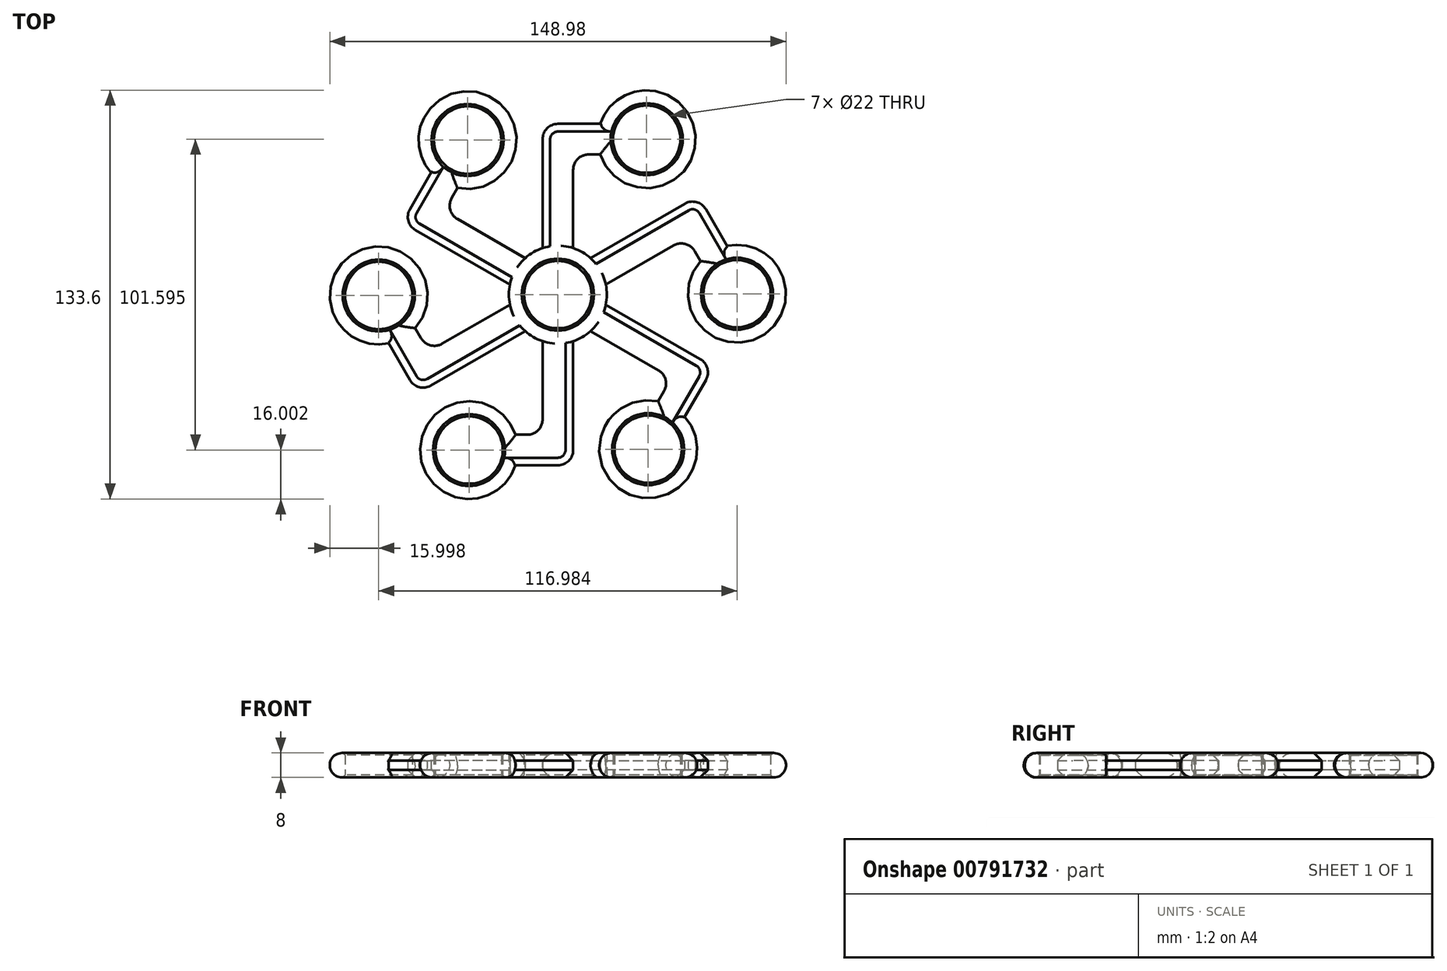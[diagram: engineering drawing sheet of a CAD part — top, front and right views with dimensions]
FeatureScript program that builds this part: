
annotation { "Feature Type Name" : "Feature", "Feature Type Description" : "" }
export const myFeature = defineFeature(function(context is Context, id is Id, definition is map)
    precondition{}
    {
        {
            var Q0;
            Q0=qCreatedBy(makeId("Top.planeOp"),FACE);
            var sketch = newSketch(context, id + "F0", { "sketchPlane" : qUnion([Q0])});
            skCircle(sketch, "E0", {"center": v(0, 0) * mm, "radius": 11 * mm});
            skCircle(sketch, "E1", {"center": v(0, 0) * mm, "radius": 16 * mm});
            skLineSegment(sketch, "E2", {"start": v(0, 0) * mm, "end": v(0, 50.8) * mm});
            skLineSegment(sketch, "E3", {"start": v(0, 50.8) * mm, "end": v(13, 50.8) * mm});
            skCircle(sketch, "E4", {"center": v(29, 50.8) * mm, "radius": 11 * mm});
            skCircle(sketch, "E5", {"center": v(29, 50.8) * mm, "radius": 16 * mm});
            skLineSegment(sketch, "E6.0", {"start": v(5, 15.2) * mm, "end": v(5, 40.8) * mm});
            skLineSegment(sketch, "E7.0", {"start": v(-5, 15.2) * mm, "end": v(-5, 50.8) * mm});
            skLineSegment(sketch, "E8.0", {"start": v(10, 45.8) * mm, "end": v(13.8, 45.8) * mm});
            skLineSegment(sketch, "E9.0", {"start": v(0, 55.8) * mm, "end": v(13.8, 55.8) * mm});
            skArc(sketch, "E10.filletArc", {"start": v(0, 55.8) * mm, "mid": v(-3.54, 54.33) * mm, "end": v(-5, 50.8) * mm});
            skArc(sketch, "E11.filletArc", {"start": v(10, 45.8) * mm, "mid": v(6.46, 44.33) * mm, "end": v(5, 40.8) * mm});
            skLineSegment(sketch, "E12", {"start": v(-5, 0) * mm, "end": v(5, 0) * mm});
            skSolve(sketch);
        }
        {
            var Q0;
            Q0=makeQuery(id+"F0.imprint","IMPRINT",FACE,{"disambiguationData":[TD([[makeQuery(id+"F0.imprint","IMPRINT",EDGE,{"derivedFrom":sQuery(id+"F0.wireOp",EDGE,"E4")}),-1.0]])]});
            var Q1;
            {var subQ1=sQuery(id+"F0.wireOp",EDGE,"E3");Q1=makeQuery(id+"F0.imprint","IMPRINT",FACE,{"disambiguationData":[TD([[makeQuery(id+"F0.imprint","IMPRINT",EDGE,{"derivedFrom":subQ1}),-1.0]])]});}
            var Q2;
            {var subQ0=sQuery(id+"F0.wireOp",EDGE,"E3");Q2=makeQuery(id+"F0.imprint","IMPRINT",FACE,{"disambiguationData":[TD([[makeQuery(id+"F0.imprint","IMPRINT",EDGE,{"derivedFrom":subQ0}),1.0]])]});}
            var Q3;
            Q3=makeQuery(id+"F0.imprint","IMPRINT",FACE,{"disambiguationData":[TD([[makeQuery(id+"F0.imprint","IMPRINT",EDGE,{"derivedFrom":sQuery(id+"F0.wireOp",EDGE,"E0")}),-1.0]])]});
            var Q4;
            Q4=qSketchRegion(id+"F2",true);
            extrude(context, id + "F1", {"entities" : qUnion([Q0, Q1, Q2, Q3, Q4]), "depth" : 8 * mm, "offsetDistance" : 25 * mm});
        }
        {
            var Q0;
            Q0=qCreatedBy(makeId("Front.planeOp"),FACE);
            var sketch = newSketch(context, id + "F2", { "sketchPlane" : qUnion([Q0])});
            skLineSegment(sketch, "E13", {"start": v(0, 0) * mm, "end": v(0, 47.95) * mm});
            skSolve(sketch);
        }
        {
            var Q0;
            Q0=makeQuery(id+"F1.opExtrude","SWEPT_BODY",BODY,{"disambiguationData":[OSD([sQuery(id+"F0.wireOp",EDGE,"E0"),sQuery(id+"F0.wireOp",EDGE,"E1"),sQuery(id+"F0.wireOp",EDGE,"E4"),sQuery(id+"F0.wireOp",EDGE,"E5"),sQuery(id+"F0.wireOp",EDGE,"E6.0"),sQuery(id+"F0.wireOp",EDGE,"E7.0"),sQuery(id+"F0.wireOp",EDGE,"E8.0"),sQuery(id+"F0.wireOp",EDGE,"E9.0"),sQuery(id+"F0.wireOp",EDGE,"E10.filletArc"),sQuery(id+"F0.wireOp",EDGE,"E11.filletArc")])]});
            var Q1;
            Q1=sQuery(id+"F2.wireOp",EDGE,"E13");
            circularPattern(context, id + "F3", {"operationType" : NewBodyOperationType.ADD, "entities" : qUnion([Q0]), "axis" : qUnion([Q1]), "angle" : 360 * degree, "instanceCount" : 6, "equalSpace" : true});
        }
        {
            var Q0;
            Q0=makeQuery(id+"F3.opPattern","COPY",EDGE,{"derivedFrom":makeQuery(id+"F1.opExtrude","CAP_EDGE",EDGE,{"disambiguationData":[OSD([sQuery(id+"F0.wireOp",EDGE,"E4")])],"isStart":false}),"instanceName":"2"});
            var Q1;
            Q1=makeQuery(id+"F3.opPattern","COPY",EDGE,{"derivedFrom":makeQuery(id+"F1.opExtrude","CAP_EDGE",EDGE,{"disambiguationData":[OSD([sQuery(id+"F0.wireOp",EDGE,"E4")])],"isStart":false}),"instanceName":"1"});
            var Q2;
            Q2=makeQuery(id+"F1.opExtrude","CAP_EDGE",EDGE,{"disambiguationData":[OSD([sQuery(id+"F0.wireOp",EDGE,"E4")])],"isStart":false});
            var Q3;
            Q3=makeQuery(id+"F3.opPattern","COPY",EDGE,{"derivedFrom":makeQuery(id+"F1.opExtrude","CAP_EDGE",EDGE,{"disambiguationData":[OSD([sQuery(id+"F0.wireOp",EDGE,"E4")])],"isStart":false}),"instanceName":"5"});
            var Q4;
            Q4=makeQuery(id+"F3.opPattern","COPY",EDGE,{"derivedFrom":makeQuery(id+"F1.opExtrude","CAP_EDGE",EDGE,{"disambiguationData":[OSD([sQuery(id+"F0.wireOp",EDGE,"E4")])],"isStart":false}),"instanceName":"3"});
            var Q5;
            Q5=makeQuery(id+"F3.opPattern","COPY",EDGE,{"derivedFrom":makeQuery(id+"F1.opExtrude","CAP_EDGE",EDGE,{"disambiguationData":[OSD([sQuery(id+"F0.wireOp",EDGE,"E4")])],"isStart":false}),"instanceName":"4"});
            var Q6;
            Q6=makeQuery(id+"F1.opExtrude","CAP_EDGE",EDGE,{"disambiguationData":[OSD([sQuery(id+"F0.wireOp",EDGE,"E0")])],"isStart":false});
            var Q7;
            Q7=makeQuery(id+"F3.opPattern","COPY",EDGE,{"derivedFrom":makeQuery(id+"F1.opExtrude","CAP_EDGE",EDGE,{"disambiguationData":[OSD([sQuery(id+"F0.wireOp",EDGE,"E4")])],"isStart":true}),"instanceName":"3"});
            var Q8;
            Q8=makeQuery(id+"F3.opPattern","COPY",EDGE,{"derivedFrom":makeQuery(id+"F1.opExtrude","CAP_EDGE",EDGE,{"disambiguationData":[OSD([sQuery(id+"F0.wireOp",EDGE,"E4")])],"isStart":true}),"instanceName":"4"});
            var Q9;
            Q9=makeQuery(id+"F3.opPattern","COPY",EDGE,{"derivedFrom":makeQuery(id+"F1.opExtrude","CAP_EDGE",EDGE,{"disambiguationData":[OSD([sQuery(id+"F0.wireOp",EDGE,"E4")])],"isStart":true}),"instanceName":"5"});
            var Q10;
            Q10=makeQuery(id+"F1.opExtrude","CAP_EDGE",EDGE,{"disambiguationData":[OSD([sQuery(id+"F0.wireOp",EDGE,"E4")])],"isStart":true});
            var Q11;
            Q11=makeQuery(id+"F3.opPattern","COPY",EDGE,{"derivedFrom":makeQuery(id+"F1.opExtrude","CAP_EDGE",EDGE,{"disambiguationData":[OSD([sQuery(id+"F0.wireOp",EDGE,"E4")])],"isStart":true}),"instanceName":"1"});
            var Q12;
            Q12=makeQuery(id+"F1.opExtrude","CAP_EDGE",EDGE,{"disambiguationData":[OSD([sQuery(id+"F0.wireOp",EDGE,"E0")])],"isStart":true});
            var Q13;
            Q13=makeQuery(id+"F3.opPattern","COPY",EDGE,{"derivedFrom":makeQuery(id+"F1.opExtrude","CAP_EDGE",EDGE,{"disambiguationData":[OSD([sQuery(id+"F0.wireOp",EDGE,"E4")])],"isStart":true}),"instanceName":"2"});
            chamfer(context, id + "F4", {"entities" : qUnion([Q0, Q1, Q2, Q3, Q4, Q5, Q6, Q7, Q8, Q9, Q10, Q11, Q12, Q13]), "width" : 0.76 * mm, "tangentPropagation" : true});
        }
        {
            var Q0;
            Q0=makeQuery(id+"F3.opPattern","COPY",EDGE,{"derivedFrom":makeQuery(id+"F1.opExtrude","CAP_EDGE",EDGE,{"disambiguationData":[OSD([sQuery(id+"F0.wireOp",EDGE,"E7.0")])],"isStart":false}),"instanceName":"3"});
            var Q1;
            Q1=makeQuery(id+"F3.opPattern","COPY",EDGE,{"derivedFrom":makeQuery(id+"F1.opExtrude","CAP_EDGE",EDGE,{"disambiguationData":[OSD([sQuery(id+"F0.wireOp",EDGE,"E7.0")])],"isStart":false}),"instanceName":"2"});
            var Q2;
            Q2=makeQuery(id+"F3.opPattern","COPY",EDGE,{"derivedFrom":makeQuery(id+"F1.opExtrude","CAP_EDGE",EDGE,{"disambiguationData":[OSD([sQuery(id+"F0.wireOp",EDGE,"E7.0")])],"isStart":false}),"instanceName":"1"});
            var Q3;
            Q3=makeQuery(id+"F1.opExtrude","CAP_EDGE",EDGE,{"disambiguationData":[OSD([sQuery(id+"F0.wireOp",EDGE,"E7.0")])],"isStart":false});
            var Q4;
            Q4=makeQuery(id+"F3.opPattern","COPY",EDGE,{"derivedFrom":makeQuery(id+"F1.opExtrude","CAP_EDGE",EDGE,{"disambiguationData":[OSD([sQuery(id+"F0.wireOp",EDGE,"E7.0")])],"isStart":false}),"instanceName":"5"});
            var Q5;
            Q5=makeQuery(id+"F3.opPattern","COPY",EDGE,{"derivedFrom":makeQuery(id+"F1.opExtrude","CAP_EDGE",EDGE,{"disambiguationData":[OSD([sQuery(id+"F0.wireOp",EDGE,"E7.0")])],"isStart":false}),"instanceName":"4"});
            var Q6;
            Q6=makeQuery(id+"F3.opPattern","COPY",EDGE,{"derivedFrom":makeQuery(id+"F1.opExtrude","CAP_EDGE",EDGE,{"disambiguationData":[OSD([sQuery(id+"F0.wireOp",EDGE,"E7.0")])],"isStart":true}),"instanceName":"3"});
            var Q7;
            Q7=makeQuery(id+"F3.opPattern","COPY",EDGE,{"derivedFrom":makeQuery(id+"F1.opExtrude","CAP_EDGE",EDGE,{"disambiguationData":[OSD([sQuery(id+"F0.wireOp",EDGE,"E7.0")])],"isStart":true}),"instanceName":"2"});
            var Q8;
            Q8=makeQuery(id+"F3.opPattern","COPY",EDGE,{"derivedFrom":makeQuery(id+"F1.opExtrude","CAP_EDGE",EDGE,{"disambiguationData":[OSD([sQuery(id+"F0.wireOp",EDGE,"E7.0")])],"isStart":true}),"instanceName":"1"});
            var Q9;
            Q9=makeQuery(id+"F1.opExtrude","CAP_EDGE",EDGE,{"disambiguationData":[OSD([sQuery(id+"F0.wireOp",EDGE,"E7.0")])],"isStart":true});
            var Q10;
            Q10=makeQuery(id+"F3.opPattern","COPY",EDGE,{"derivedFrom":makeQuery(id+"F1.opExtrude","CAP_EDGE",EDGE,{"disambiguationData":[OSD([sQuery(id+"F0.wireOp",EDGE,"E7.0")])],"isStart":true}),"instanceName":"5"});
            var Q11;
            Q11=makeQuery(id+"F3.opPattern","COPY",EDGE,{"derivedFrom":makeQuery(id+"F1.opExtrude","CAP_EDGE",EDGE,{"disambiguationData":[OSD([sQuery(id+"F0.wireOp",EDGE,"E7.0")])],"isStart":true}),"instanceName":"4"});
            chamfer(context, id + "F5", {"entities" : qUnion([Q0, Q1, Q2, Q3, Q4, Q5, Q6, Q7, Q8, Q9, Q10, Q11]), "width" : 2.5 * mm, "tangentPropagation" : true});
        }
        {
            var Q0;
            Q0=makeQuery(id+"F3.opPattern","COPY",EDGE,{"derivedFrom":makeQuery(id+"F1.opExtrude","CAP_EDGE",EDGE,{"disambiguationData":[OSD([sQuery(id+"F0.wireOp",EDGE,"E6.0")])],"isStart":true}),"instanceName":"2"});
            var Q1;
            Q1=makeQuery(id+"F3.opPattern","COPY",EDGE,{"derivedFrom":makeQuery(id+"F1.opExtrude","CAP_EDGE",EDGE,{"disambiguationData":[OSD([sQuery(id+"F0.wireOp",EDGE,"E6.0")])],"isStart":true}),"instanceName":"1"});
            var Q2;
            Q2=makeQuery(id+"F1.opExtrude","CAP_EDGE",EDGE,{"disambiguationData":[OSD([sQuery(id+"F0.wireOp",EDGE,"E6.0")])],"isStart":true});
            var Q3;
            Q3=makeQuery(id+"F3.opPattern","COPY",EDGE,{"derivedFrom":makeQuery(id+"F1.opExtrude","CAP_EDGE",EDGE,{"disambiguationData":[OSD([sQuery(id+"F0.wireOp",EDGE,"E6.0")])],"isStart":true}),"instanceName":"5"});
            var Q4;
            Q4=makeQuery(id+"F3.opPattern","COPY",EDGE,{"derivedFrom":makeQuery(id+"F1.opExtrude","CAP_EDGE",EDGE,{"disambiguationData":[OSD([sQuery(id+"F0.wireOp",EDGE,"E6.0")])],"isStart":true}),"instanceName":"4"});
            var Q5;
            Q5=makeQuery(id+"F3.opPattern","COPY",EDGE,{"derivedFrom":makeQuery(id+"F1.opExtrude","CAP_EDGE",EDGE,{"disambiguationData":[OSD([sQuery(id+"F0.wireOp",EDGE,"E6.0")])],"isStart":true}),"instanceName":"3"});
            var Q6;
            Q6=makeQuery(id+"F3.opPattern","COPY",EDGE,{"derivedFrom":makeQuery(id+"F1.opExtrude","CAP_EDGE",EDGE,{"disambiguationData":[OSD([sQuery(id+"F0.wireOp",EDGE,"E6.0")])],"isStart":false}),"instanceName":"2"});
            var Q7;
            Q7=makeQuery(id+"F3.opPattern","COPY",EDGE,{"derivedFrom":makeQuery(id+"F1.opExtrude","CAP_EDGE",EDGE,{"disambiguationData":[OSD([sQuery(id+"F0.wireOp",EDGE,"E6.0")])],"isStart":false}),"instanceName":"1"});
            var Q8;
            Q8=makeQuery(id+"F1.opExtrude","CAP_EDGE",EDGE,{"disambiguationData":[OSD([sQuery(id+"F0.wireOp",EDGE,"E6.0")])],"isStart":false});
            var Q9;
            Q9=makeQuery(id+"F3.opPattern","COPY",EDGE,{"derivedFrom":makeQuery(id+"F1.opExtrude","CAP_EDGE",EDGE,{"disambiguationData":[OSD([sQuery(id+"F0.wireOp",EDGE,"E6.0")])],"isStart":false}),"instanceName":"5"});
            var Q10;
            Q10=makeQuery(id+"F3.opPattern","COPY",EDGE,{"derivedFrom":makeQuery(id+"F1.opExtrude","CAP_EDGE",EDGE,{"disambiguationData":[OSD([sQuery(id+"F0.wireOp",EDGE,"E6.0")])],"isStart":false}),"instanceName":"4"});
            var Q11;
            Q11=makeQuery(id+"F3.opPattern","COPY",EDGE,{"derivedFrom":makeQuery(id+"F1.opExtrude","CAP_EDGE",EDGE,{"disambiguationData":[OSD([sQuery(id+"F0.wireOp",EDGE,"E6.0")])],"isStart":false}),"instanceName":"3"});
            var Q12;
            Q12=makeQuery(id+"F3.opPattern","COPY",EDGE,{"derivedFrom":makeQuery(id+"F1.opExtrude","CAP_EDGE",EDGE,{"disambiguationData":[OSD([sQuery(id+"F0.wireOp",EDGE,"E5")])],"isStart":false}),"instanceName":"1"});
            var Q13;
            Q13=makeQuery(id+"F3.opPattern","COPY",EDGE,{"derivedFrom":makeQuery(id+"F1.opExtrude","CAP_EDGE",EDGE,{"disambiguationData":[OSD([sQuery(id+"F0.wireOp",EDGE,"E5")])],"isStart":true}),"instanceName":"1"});
            var Q14;
            Q14=makeQuery(id+"F3.opPattern","COPY",EDGE,{"derivedFrom":makeQuery(id+"F1.opExtrude","CAP_EDGE",EDGE,{"disambiguationData":[OSD([sQuery(id+"F0.wireOp",EDGE,"E5")])],"isStart":false}),"instanceName":"2"});
            var Q15;
            Q15=makeQuery(id+"F3.opPattern","COPY",EDGE,{"derivedFrom":makeQuery(id+"F1.opExtrude","CAP_EDGE",EDGE,{"disambiguationData":[OSD([sQuery(id+"F0.wireOp",EDGE,"E5")])],"isStart":true}),"instanceName":"2"});
            var Q16;
            Q16=makeQuery(id+"F1.opExtrude","CAP_EDGE",EDGE,{"disambiguationData":[OSD([sQuery(id+"F0.wireOp",EDGE,"E5")])],"isStart":false});
            var Q17;
            Q17=makeQuery(id+"F1.opExtrude","CAP_EDGE",EDGE,{"disambiguationData":[OSD([sQuery(id+"F0.wireOp",EDGE,"E5")])],"isStart":true});
            var Q18;
            Q18=makeQuery(id+"F3.opPattern","COPY",EDGE,{"derivedFrom":makeQuery(id+"F1.opExtrude","CAP_EDGE",EDGE,{"disambiguationData":[OSD([sQuery(id+"F0.wireOp",EDGE,"E5")])],"isStart":false}),"instanceName":"5"});
            var Q19;
            Q19=makeQuery(id+"F3.opPattern","COPY",EDGE,{"derivedFrom":makeQuery(id+"F1.opExtrude","CAP_EDGE",EDGE,{"disambiguationData":[OSD([sQuery(id+"F0.wireOp",EDGE,"E5")])],"isStart":true}),"instanceName":"5"});
            var Q20;
            Q20=makeQuery(id+"F3.opPattern","COPY",EDGE,{"derivedFrom":makeQuery(id+"F1.opExtrude","CAP_EDGE",EDGE,{"disambiguationData":[OSD([sQuery(id+"F0.wireOp",EDGE,"E5")])],"isStart":false}),"instanceName":"4"});
            var Q21;
            Q21=makeQuery(id+"F3.opPattern","COPY",EDGE,{"derivedFrom":makeQuery(id+"F1.opExtrude","CAP_EDGE",EDGE,{"disambiguationData":[OSD([sQuery(id+"F0.wireOp",EDGE,"E5")])],"isStart":true}),"instanceName":"4"});
            var Q22;
            Q22=makeQuery(id+"F3.opPattern","COPY",EDGE,{"derivedFrom":makeQuery(id+"F1.opExtrude","CAP_EDGE",EDGE,{"disambiguationData":[OSD([sQuery(id+"F0.wireOp",EDGE,"E5")])],"isStart":false}),"instanceName":"3"});
            var Q23;
            Q23=makeQuery(id+"F3.opPattern","COPY",EDGE,{"derivedFrom":makeQuery(id+"F1.opExtrude","CAP_EDGE",EDGE,{"disambiguationData":[OSD([sQuery(id+"F0.wireOp",EDGE,"E5")])],"isStart":true}),"instanceName":"3"});
            fillet(context, id + "F6", {"entities" : qUnion([Q0, Q1, Q2, Q3, Q4, Q5, Q6, Q7, Q8, Q9, Q10, Q11, Q12, Q13, Q14, Q15, Q16, Q17, Q18, Q19, Q20, Q21, Q22, Q23]), "radius" : 4 * mm, "tangentPropagation" : true, "allowEdgeOverflow" : false});
        }
    });
